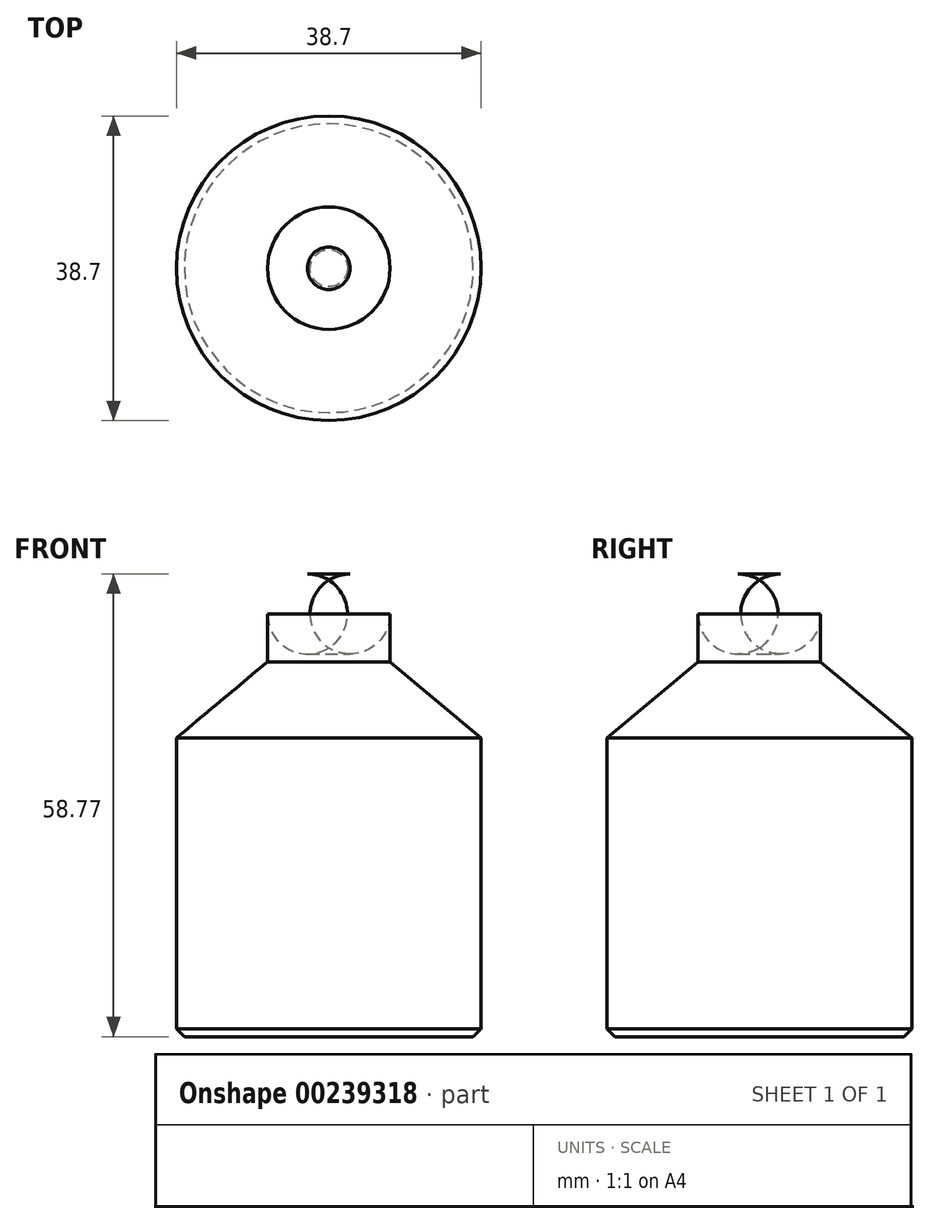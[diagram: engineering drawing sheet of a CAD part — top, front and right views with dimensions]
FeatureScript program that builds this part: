
annotation { "Feature Type Name" : "Feature", "Feature Type Description" : "" }
export const myFeature = defineFeature(function(context is Context, id is Id, definition is map)
    precondition{}
    {
        {
            var Q0;
            Q0=qCreatedBy(makeId("Front.planeOp"),FACE);
            var sketch = newSketch(context, id + "F0", { "sketchPlane" : qUnion([Q0])});
            skLineSegment(sketch, "E0", {"start": v(0, 58.77) * mm, "end": v(7.78, 58.77) * mm});
            skLineSegment(sketch, "E1", {"start": v(7.78, 58.77) * mm, "end": v(7.78, 47.63) * mm});
            skLineSegment(sketch, "E2", {"start": v(7.78, 47.63) * mm, "end": v(19.35, 37.95) * mm});
            skLineSegment(sketch, "E3", {"start": v(19.35, 37.95) * mm, "end": v(19.35, 0) * mm});
            skLineSegment(sketch, "E4", {"start": v(19.35, 0) * mm, "end": v(0, 0) * mm});
            skLineSegment(sketch, "E5", {"start": v(0, 0) * mm, "end": v(0, 58.77) * mm});
            skSolve(sketch);
        }
        {
            var Q0;
            Q0=makeQuery(id+"F0.imprint","IMPRINT",FACE,{"disambiguationData":[TD([[makeQuery(id+"F0.imprint","IMPRINT",EDGE,{"derivedFrom":sQuery(id+"F0.wireOp",EDGE,"E0")}),-1.0]])]});
            var Q1;
            Q1=sQuery(id+"F0.wireOp",EDGE,"E5");
            revolve(context, id + "F1", {"entities" : qUnion([Q0]), "axis" : qUnion([Q1]), "revolveType" : RevolveType.FULL});
        }
        {
            var Q0;
            Q0=makeQuery(id+"F1.opRevolve","SWEPT_EDGE",EDGE,{"disambiguationData":[OSD([sQuery(id+"F0.wireOp",EDGE,"E0"),sQuery(id+"F0.wireOp",EDGE,"E1")])]});
            fillet(context, id + "F2", {"entities" : qUnion([Q0]), "radius" : 5.08 * mm, "tangentPropagation" : true, "allowEdgeOverflow" : false});
        }
        {
            var Q0;
            Q0=makeQuery(id+"F1.opRevolve","SWEPT_EDGE",EDGE,{"disambiguationData":[OSD([sQuery(id+"F0.wireOp",EDGE,"E3"),sQuery(id+"F0.wireOp",EDGE,"E4")])]});
            chamfer(context, id + "F3", {"entities" : qUnion([Q0]), "width" : 1 * mm, "tangentPropagation" : true});
        }
    });
